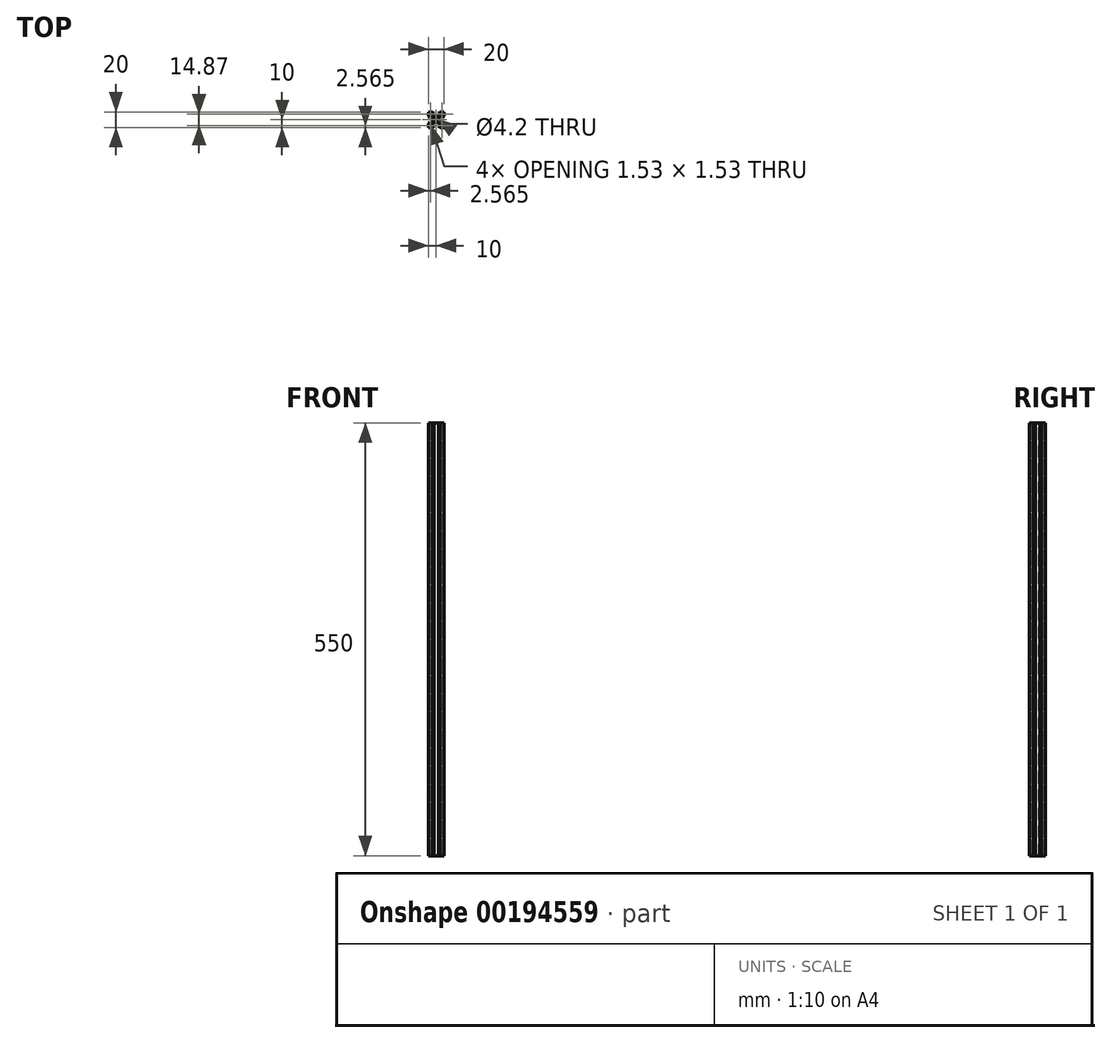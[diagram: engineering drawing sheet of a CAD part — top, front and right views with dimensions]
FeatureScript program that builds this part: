
annotation { "Feature Type Name" : "Feature", "Feature Type Description" : "" }
export const myFeature = defineFeature(function(context is Context, id is Id, definition is map)
    precondition{}
    {
        {
            var Q0;
            Q0=qCreatedBy(makeId("Top.planeOp"),FACE);
            var sketch = newSketch(context, id + "F0", { "sketchPlane" : qUnion([Q0])});
            skLineSegment(sketch, "E0.bottom", {"start": v(0, 0) * mm, "end": v(5.2, 0) * mm});
            skLineSegment(sketch, "E0.top", {"start": v(0, 20) * mm, "end": v(5.2, 20) * mm});
            skLineSegment(sketch, "E0.left", {"start": v(0, 0) * mm, "end": v(0, 5.2) * mm});
            skLineSegment(sketch, "E0.right", {"start": v(20, 0) * mm, "end": v(20, 5.2) * mm});
            skLineSegment(sketch, "E1", {"start": v(20, 5.2) * mm, "end": v(18.2, 7) * mm});
            skLineSegment(sketch, "E2", {"start": v(18.2, 7) * mm, "end": v(18.2, 4.4) * mm});
            skLineSegment(sketch, "E3", {"start": v(18.2, 4.4) * mm, "end": v(16.56, 4.4) * mm});
            skLineSegment(sketch, "E4", {"start": v(16.56, 4.4) * mm, "end": v(13.8, 7.16) * mm});
            skLineSegment(sketch, "E5", {"start": v(13.8, 7.16) * mm, "end": v(13.8, 12.84) * mm});
            skLineSegment(sketch, "E6", {"start": v(13.8, 12.84) * mm, "end": v(16.56, 15.6) * mm});
            skLineSegment(sketch, "E7", {"start": v(16.56, 15.6) * mm, "end": v(18.2, 15.6) * mm});
            skLineSegment(sketch, "E8", {"start": v(18.2, 15.6) * mm, "end": v(18.2, 13) * mm});
            skLineSegment(sketch, "E9", {"start": v(18.2, 13) * mm, "end": v(20, 14.8) * mm});
            skPoint(sketch, "E10.centerSnap0", {"position": v(13.8, 10) * mm});
            skLineSegment(sketch, "E11.trimOffspring", {"start": v(20, 14.8) * mm, "end": v(20, 20) * mm});
            skLineSegment(sketch, "E12", {"start": v(14.8, 20) * mm, "end": v(13, 18.2) * mm});
            skLineSegment(sketch, "E13", {"start": v(13, 18.2) * mm, "end": v(15.6, 18.2) * mm});
            skLineSegment(sketch, "E14", {"start": v(15.6, 18.2) * mm, "end": v(15.6, 16.56) * mm});
            skLineSegment(sketch, "E15", {"start": v(15.6, 16.56) * mm, "end": v(12.84, 13.8) * mm});
            skLineSegment(sketch, "E16", {"start": v(12.84, 13.8) * mm, "end": v(7.16, 13.8) * mm});
            skLineSegment(sketch, "E17", {"start": v(7.16, 13.8) * mm, "end": v(4.4, 16.56) * mm});
            skLineSegment(sketch, "E18", {"start": v(4.4, 16.56) * mm, "end": v(4.4, 18.2) * mm});
            skLineSegment(sketch, "E19", {"start": v(4.4, 18.2) * mm, "end": v(7, 18.2) * mm});
            skLineSegment(sketch, "E20", {"start": v(7, 18.2) * mm, "end": v(5.2, 20) * mm});
            skLineSegment(sketch, "E21.trimOffspring", {"start": v(14.8, 20) * mm, "end": v(20, 20) * mm});
            skLineSegment(sketch, "E22", {"start": v(14.8, 0) * mm, "end": v(13, 1.8) * mm});
            skLineSegment(sketch, "E23", {"start": v(13, 1.8) * mm, "end": v(15.6, 1.8) * mm});
            skLineSegment(sketch, "E24", {"start": v(15.6, 1.8) * mm, "end": v(15.6, 3.44) * mm});
            skLineSegment(sketch, "E25", {"start": v(15.6, 3.44) * mm, "end": v(12.84, 6.2) * mm});
            skLineSegment(sketch, "E26", {"start": v(12.84, 6.2) * mm, "end": v(7.16, 6.2) * mm});
            skLineSegment(sketch, "E27", {"start": v(7.16, 6.2) * mm, "end": v(4.4, 3.44) * mm});
            skLineSegment(sketch, "E28", {"start": v(4.4, 3.44) * mm, "end": v(4.4, 1.8) * mm});
            skLineSegment(sketch, "E29", {"start": v(4.4, 1.8) * mm, "end": v(7, 1.8) * mm});
            skLineSegment(sketch, "E30", {"start": v(7, 1.8) * mm, "end": v(5.2, 0) * mm});
            skLineSegment(sketch, "E31", {"start": v(0, 14.8) * mm, "end": v(1.8, 13) * mm});
            skLineSegment(sketch, "E32", {"start": v(1.8, 13) * mm, "end": v(1.8, 15.6) * mm});
            skLineSegment(sketch, "E33", {"start": v(1.8, 15.6) * mm, "end": v(3.44, 15.6) * mm});
            skLineSegment(sketch, "E34", {"start": v(3.44, 15.6) * mm, "end": v(6.2, 12.84) * mm});
            skLineSegment(sketch, "E35", {"start": v(6.2, 12.84) * mm, "end": v(6.2, 7.16) * mm});
            skLineSegment(sketch, "E36", {"start": v(6.2, 7.16) * mm, "end": v(3.44, 4.4) * mm});
            skLineSegment(sketch, "E37", {"start": v(3.44, 4.4) * mm, "end": v(1.8, 4.4) * mm});
            skLineSegment(sketch, "E38", {"start": v(1.8, 4.4) * mm, "end": v(1.8, 7) * mm});
            skLineSegment(sketch, "E39", {"start": v(1.8, 7) * mm, "end": v(0, 5.2) * mm});
            skLineSegment(sketch, "E40.trimOffspring", {"start": v(0, 14.8) * mm, "end": v(0, 20) * mm});
            skLineSegment(sketch, "E41.trimOffspring", {"start": v(14.8, 0) * mm, "end": v(20, 0) * mm});
            skSolve(sketch);
        }
        {
            var Q0;
            Q0 = qSketchRegion(id + "F0", true);
            extrude(context, id + "F1", {"entities" : qUnion([Q0]), "depth" : 550 * mm});
        }
        {
            var Q0;
            Q0=makeQuery(id+"F1.opExtrude","CAP_FACE",FACE,{"disambiguationData":[OSD([sQuery(id+"F0.wireOp",EDGE,"E0.bottom"),sQuery(id+"F0.wireOp",EDGE,"E0.top"),sQuery(id+"F0.wireOp",EDGE,"E0.left"),sQuery(id+"F0.wireOp",EDGE,"E0.right"),sQuery(id+"F0.wireOp",EDGE,"E1"),sQuery(id+"F0.wireOp",EDGE,"E2"),sQuery(id+"F0.wireOp",EDGE,"E3"),sQuery(id+"F0.wireOp",EDGE,"E4"),sQuery(id+"F0.wireOp",EDGE,"E5"),sQuery(id+"F0.wireOp",EDGE,"E6"),sQuery(id+"F0.wireOp",EDGE,"E7"),sQuery(id+"F0.wireOp",EDGE,"E8"),sQuery(id+"F0.wireOp",EDGE,"E9"),sQuery(id+"F0.wireOp",EDGE,"E11.trimOffspring"),sQuery(id+"F0.wireOp",EDGE,"E12"),sQuery(id+"F0.wireOp",EDGE,"E13"),sQuery(id+"F0.wireOp",EDGE,"E14"),sQuery(id+"F0.wireOp",EDGE,"E15"),sQuery(id+"F0.wireOp",EDGE,"E16"),sQuery(id+"F0.wireOp",EDGE,"E17"),sQuery(id+"F0.wireOp",EDGE,"E18"),sQuery(id+"F0.wireOp",EDGE,"E19"),sQuery(id+"F0.wireOp",EDGE,"E20"),sQuery(id+"F0.wireOp",EDGE,"E21.trimOffspring"),sQuery(id+"F0.wireOp",EDGE,"E22"),sQuery(id+"F0.wireOp",EDGE,"E23"),sQuery(id+"F0.wireOp",EDGE,"E24"),sQuery(id+"F0.wireOp",EDGE,"E25"),sQuery(id+"F0.wireOp",EDGE,"E26"),sQuery(id+"F0.wireOp",EDGE,"E27"),sQuery(id+"F0.wireOp",EDGE,"E28"),sQuery(id+"F0.wireOp",EDGE,"E29"),sQuery(id+"F0.wireOp",EDGE,"E30"),sQuery(id+"F0.wireOp",EDGE,"E31"),sQuery(id+"F0.wireOp",EDGE,"E32"),sQuery(id+"F0.wireOp",EDGE,"E33"),sQuery(id+"F0.wireOp",EDGE,"E34"),sQuery(id+"F0.wireOp",EDGE,"E35"),sQuery(id+"F0.wireOp",EDGE,"E36"),sQuery(id+"F0.wireOp",EDGE,"E37"),sQuery(id+"F0.wireOp",EDGE,"E38"),sQuery(id+"F0.wireOp",EDGE,"E39"),sQuery(id+"F0.wireOp",EDGE,"E40.trimOffspring"),sQuery(id+"F0.wireOp",EDGE,"E41.trimOffspring")])],"isStart":false});
            var sketch = newSketch(context, id + "F2", { "sketchPlane" : qUnion([Q0])});
            skCircle(sketch, "E42", {"center": v(10, 10) * mm, "radius": 2.1 * mm});
            skPoint(sketch, "E42.centerSnap0", {"position": v(10, 13.8) * mm});
            skPoint(sketch, "E42.centerSnap1", {"position": v(13.8, 10) * mm});
            skLineSegment(sketch, "E43", {"start": v(18.2, 18.2) * mm, "end": v(16.67, 18.2) * mm});
            skLineSegment(sketch, "E44", {"start": v(16.67, 18.2) * mm, "end": v(18.2, 16.67) * mm});
            skLineSegment(sketch, "E45", {"start": v(18.2, 16.67) * mm, "end": v(18.2, 18.2) * mm});
            skLineSegment(sketch, "E46", {"start": v(1.8, 18.2) * mm, "end": v(1.8, 16.67) * mm});
            skLineSegment(sketch, "E47", {"start": v(1.8, 16.67) * mm, "end": v(3.33, 18.2) * mm});
            skLineSegment(sketch, "E48", {"start": v(3.33, 18.2) * mm, "end": v(1.8, 18.2) * mm});
            skLineSegment(sketch, "E49", {"start": v(1.8, 1.8) * mm, "end": v(3.33, 1.8) * mm});
            skLineSegment(sketch, "E50", {"start": v(3.33, 1.8) * mm, "end": v(1.8, 3.33) * mm});
            skLineSegment(sketch, "E51", {"start": v(1.8, 3.33) * mm, "end": v(1.8, 1.8) * mm});
            skLineSegment(sketch, "E52", {"start": v(18.2, 1.8) * mm, "end": v(18.2, 3.33) * mm});
            skLineSegment(sketch, "E53", {"start": v(18.2, 3.33) * mm, "end": v(16.67, 1.8) * mm});
            skLineSegment(sketch, "E54", {"start": v(16.67, 1.8) * mm, "end": v(18.2, 1.8) * mm});
            skSolve(sketch);
        }
        {
            var Q0;
            Q0 = qSketchRegion(id + "F2", true);
            extrude(context, id + "F3", {"entities" : qUnion([Q0]), "operationType" : NewBodyOperationType.REMOVE, "endBound" : BoundingType.THROUGH_ALL, "oppositeDirection" : true, "depth" : 25 * mm});
        }
    });
